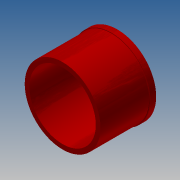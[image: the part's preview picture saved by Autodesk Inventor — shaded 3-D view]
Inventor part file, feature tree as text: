
AUTODESK INVENTOR PART (.ipt)
format: ipt  version: 2017.3 (Build 213257000, 257)  size: 118,272 bytes
history: native  units: in
note: dims shown in document units (in); Inventor stores cm internally (conversion verified against a paired STEP export)
features: other x3, extrude x2, sketch x2
ambient origin geometry x8: Origin, YZ Plane, XZ Plane, XY Plane, X Axis, Y Axis, Z Axis, Center Point
bodies: Solid1 (feature_tree)
feature tree (7):
  other  "A1-19027-100-06 HCWI liner - pup.ipt"
  extrude  "Extrusion1"  Depth=0.5in TaperAngle=0.0deg
  extrude  "Extrusion2"  Depth=0.5in
  other  "Solid1::A1-19027-100-06 HCWI liner - pup.ipt"
  other  "TaggingFeature1"
  sketch  "Sketch2"  dims[d0=0.3937in d1=0.5in d2=2.0in d3=0.0in d4=0.0in]
  sketch  "Sketch3"  dims[d5=0.5in d6=0.5in d7=0.0in d8=0.0in d9=0.25in]
